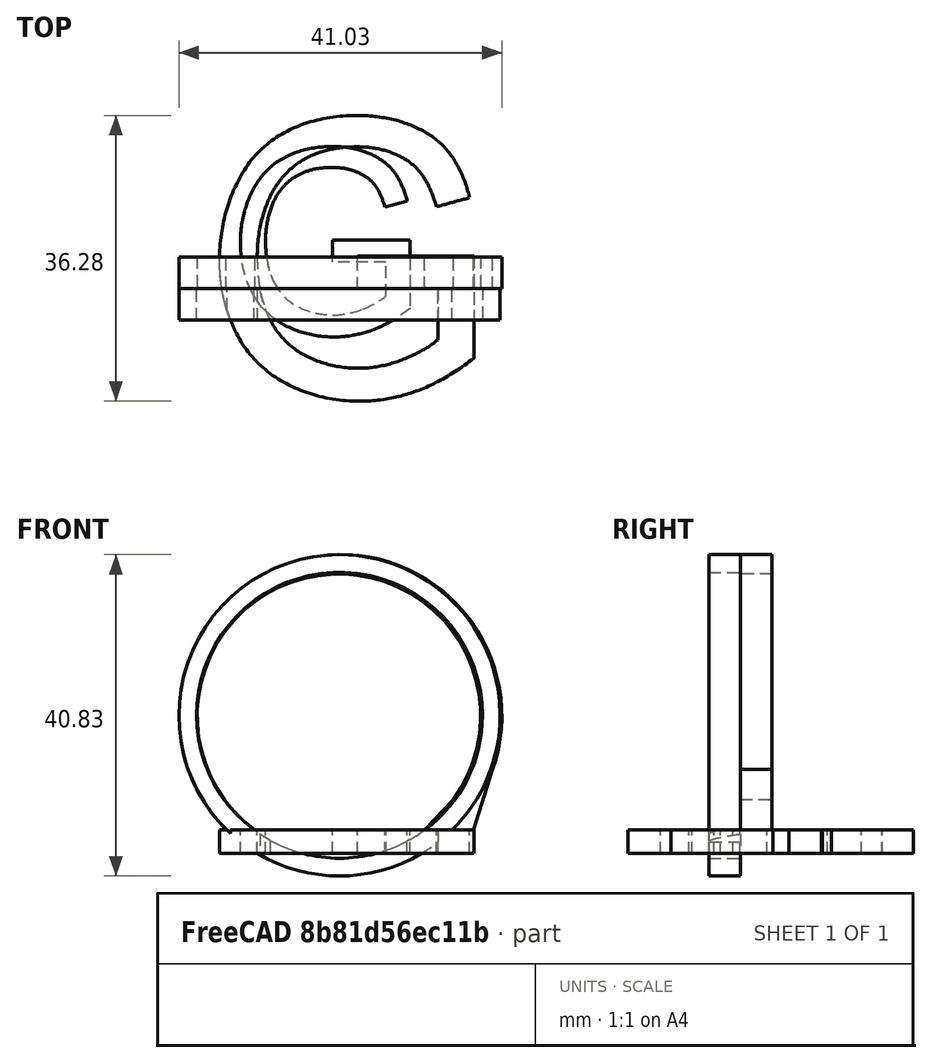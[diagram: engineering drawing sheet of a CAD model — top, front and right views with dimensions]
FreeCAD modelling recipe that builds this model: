
FCSTD DOCUMENT  (FreeCAD 0.21R33668 +26 (Git))
Label: Rings
License: All rights reserved
LicenseURL: https://en.wikipedia.org/wiki/All_rights_reserved
objects: PartDesign::Pad×4, PartDesign::Body×3, Sketcher::SketchObject×2, Part::Part2DObjectPython×1, Part::FeaturePython×1, Part::Fuse×1
note: 16 computed .brp shape members not serialized (recipe doc carries the construction recipe); baked Part::Feature solids carry a one-line shape summary decoded from their .brp

FEATURE [Part::Part2DObjectPython] ShapeString001  # Draft 2D object (typed FeaturePython)
  FontFile = <path>
  MakeFace = true
  Placement = pos=(-13.28,-10.75,10) rot=(0,0,1;0rad)
  Size = 25
  String = G
  Tracking = 0
FEATURE [PartDesign::Pad] Pad001
  Direction = (0,0,1)
  Length = 3
  Length2 = 10
  Placement = pos=(-13.28,-10.75,10) rot=(0,0,1;0rad)
  Profile = -> ShapeString001
  ReferenceAxis = -> ShapeString001 [N_Axis]
  Type = 0
FEATURE [PartDesign::Body] Body
  Group = -> [Pad001,ShapeString001]
  Origin = -> Origin
  Placement = pos=(0,3.8,-10) rot=(0,0,1;0rad)
  Tip = -> Pad001
FEATURE [Sketcher::SketchObject] Sketch
  FullyConstrained = false
  MapMode = 5
  Support = -> [XY_Plane001]
  sketch-geometry (6):
    g0: ArcOfCircle CenterX=-0.108993 CenterY=4.374e-12 CenterZ=0 NormalX=0 NormalY=0 NormalZ=1 AngleXU=0 Radius=18.0005 StartAngle=2.20292 EndAngle=6.91263
    g1: ArcOfCircle CenterX=0.0873921 CenterY=0.0168834 CenterZ=0 NormalX=0 NormalY=0 NormalZ=1 AngleXU=0 Radius=20.5017 StartAngle=2.3556 EndAngle=6.62166
    g2: LineSegment StartX=-14.401 StartY=14.5223 StartZ=0 EndX=-10.7447 EndY=14.5223 EndZ=0
    g3: LineSegment StartX=14.4418 StartY=10.5967 StartZ=0 EndX=10.7532 EndY=14.5232 EndZ=0
    g4: LineSegment StartX=16.9542 StartY=14.5232 StartZ=0 EndX=19.4259 EndY=6.82453 EndZ=0
    g5: LineSegment StartX=10.7532 StartY=14.5232 StartZ=0 EndX=16.9542 EndY=14.5232 EndZ=0
  constraints (8):
    c: Horizontal(g2)
    c: Coincident(g1,g2)
    c: Coincident(g0,g2)
    c: Coincident(g3,g0)
    c: Coincident(g1,g4)
    c: Coincident(g5,g3)
    c: Coincident(g5,g4)
    c: Horizontal(g5)
FEATURE [PartDesign::Pad] Pad
  Direction = (0,0,1)
  Length = 4
  Length2 = 10
  Profile = -> Sketch
  ReferenceAxis = -> Sketch [N_Axis]
  Type = 0
FEATURE [PartDesign::Body] Body001
  Group = -> [Sketch,Pad]
  Origin = -> Origin001
  Placement = pos=(1.1,-1.2,17.5) rot=(-1,0,0;1.5708rad)
  Tip = -> Pad
FEATURE [Part::FeaturePython] Clone  label="Pad003"  # Draft clone (typed FeaturePython)
  AttacherType = Attacher::AttachEngine3D
  Fuse = false
  Objects = -> [Pad001]
  Placement = pos=(-16.8162,-14.899,0) rot=(0,0,1;0rad)
  Scale = (1.5,1.5,1)
FEATURE [Part::Fuse] Fusion  label="G Ring"
  Base = -> Body001
  Tool = -> Clone
FEATURE [Sketcher::SketchObject] Sketch001
  FullyConstrained = false
  MapMode = 5
  Placement = pos=(0,-1.2,0) rot=(1,0,0;1.5708rad)
  Support = -> [Fusion]
  sketch-geometry (2):
    g0: Circle CenterX=1.0733 CenterY=17.5588 CenterZ=0 NormalX=0 NormalY=0 NormalZ=1 AngleXU=0 Radius=20.4106
    g1: Circle CenterX=1.0733 CenterY=17.5588 CenterZ=0 NormalX=0 NormalY=0 NormalZ=1 AngleXU=0 Radius=18.1569
  constraints (1):
    c: Coincident(g1,g0)
FEATURE [PartDesign::Pad] Pad002
  Direction = (0,-1,2e-16)
  Length = 4
  Length2 = 10
  Profile = -> Sketch001
  ReferenceAxis = -> Sketch001 [N_Axis]
  Type = 0
FEATURE [PartDesign::Pad] Pad003  label="Pad004"
  BaseFeature = -> Pad002
  Direction = (0,-1,2e-16)
  Length = 4
  Length2 = 10
  Profile = -> Sketch001
  ReferenceAxis = -> Sketch001 [N_Axis]
  Type = 0
FEATURE [PartDesign::Body] Body002  label="Base Ring"
  Group = -> [Sketch001,Pad002,Pad003]
  Origin = -> Origin002
  Tip = -> Pad003
note: 1 file-system path scrubbed to <path> (originals preserved in the JSON sidecar)
